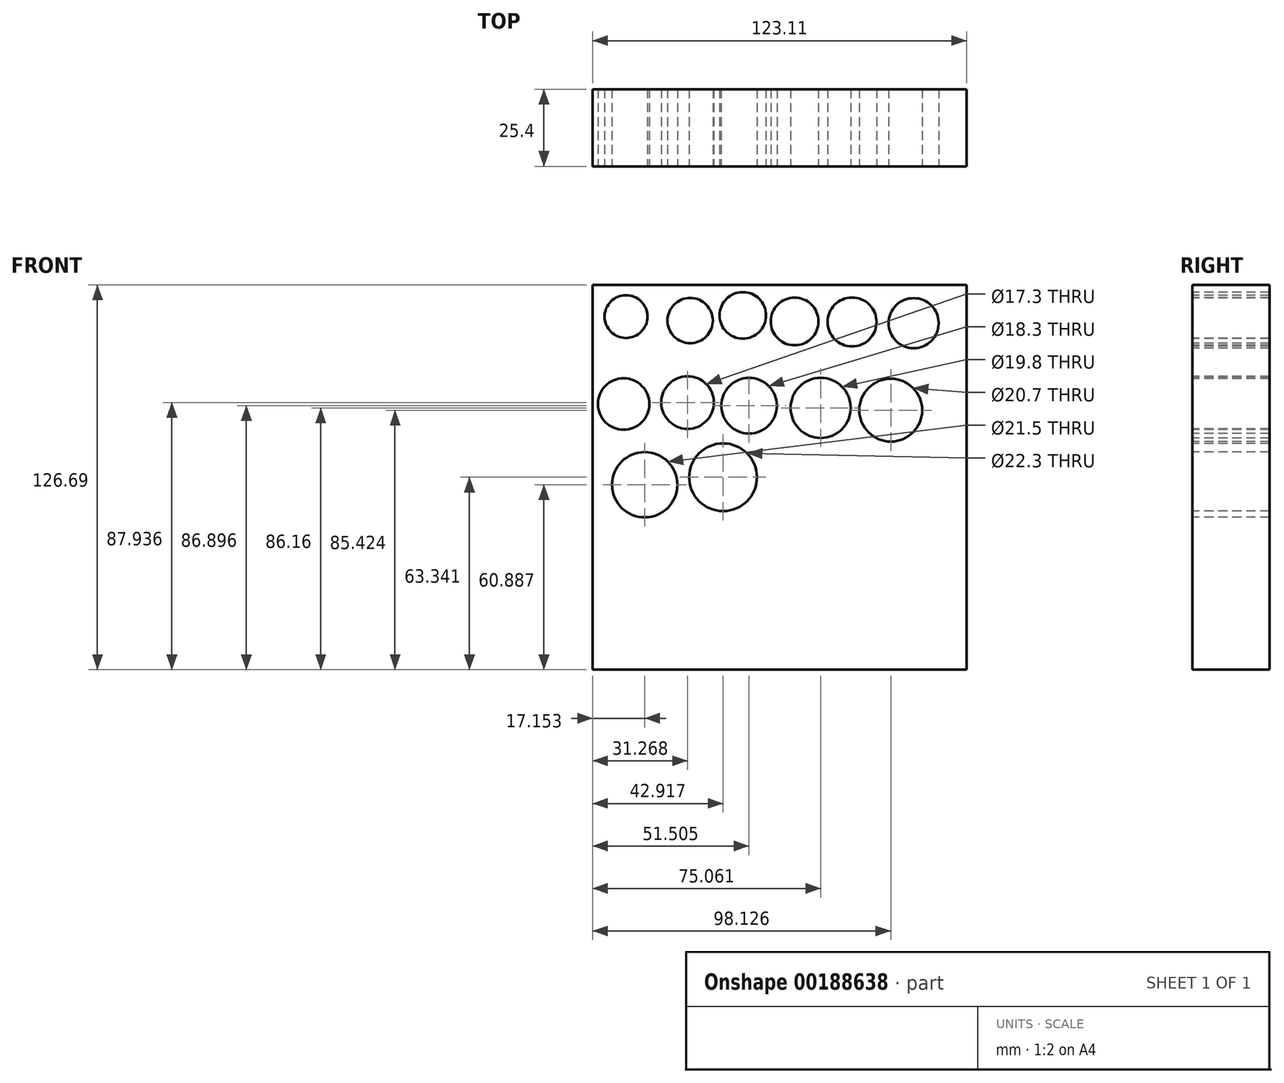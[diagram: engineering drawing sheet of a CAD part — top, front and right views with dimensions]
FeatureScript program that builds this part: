
annotation { "Feature Type Name" : "Feature", "Feature Type Description" : "" }
export const myFeature = defineFeature(function(context is Context, id is Id, definition is map)
    precondition{}
    {
        {
            var Q0;
            Q0=qCreatedBy(makeId("Front.planeOp"),FACE);
            var sketch = newSketch(context, id + "F0", { "sketchPlane" : qUnion([Q0])});
            skLineSegment(sketch, "E0.bottom", {"start": v(-58.66, 60.18) * mm, "end": v(64.45, 60.18) * mm});
            skLineSegment(sketch, "E0.top", {"start": v(-58.66, -66.51) * mm, "end": v(64.45, -66.51) * mm});
            skLineSegment(sketch, "E0.left", {"start": v(-58.66, 60.18) * mm, "end": v(-58.66, -66.51) * mm});
            skLineSegment(sketch, "E0.right", {"start": v(64.45, 60.18) * mm, "end": v(64.45, -66.51) * mm});
            skSolve(sketch);
        }
        {
            var Q0;
            Q0=makeQuery(id+"F0.imprint","IMPRINT",FACE,{"disambiguationData":[TD([[makeQuery(id+"F0.imprint","IMPRINT",EDGE,{"derivedFrom":sQuery(id+"F0.wireOp",EDGE,"E0.bottom")}),-1.0]])]});
            extrude(context, id + "F1", {"entities" : qUnion([Q0]), "depth" : 25.4 * mm});
        }
        {
            var Q0;
            Q0=makeQuery(id+"F1.opExtrude","CAP_FACE",FACE,{"disambiguationData":[OSD([sQuery(id+"F0.wireOp",EDGE,"E0.bottom"),sQuery(id+"F0.wireOp",EDGE,"E0.top"),sQuery(id+"F0.wireOp",EDGE,"E0.left"),sQuery(id+"F0.wireOp",EDGE,"E0.right")])],"isStart":false});
            var sketch = newSketch(context, id + "F2", { "sketchPlane" : qUnion([Q0])});
            skCircle(sketch, "E1", {"center": v(-47.65, 49.71) * mm, "radius": 7.05 * mm});
            skCircle(sketch, "E2", {"center": v(-26.54, 48.4) * mm, "radius": 7.45 * mm});
            skCircle(sketch, "E3", {"center": v(-9.22, 50.1) * mm, "radius": 7.65 * mm});
            skCircle(sketch, "E4", {"center": v(7.81, 48.11) * mm, "radius": 7.85 * mm});
            skCircle(sketch, "E5", {"center": v(26.72, 47.94) * mm, "radius": 8.05 * mm});
            skCircle(sketch, "E6", {"center": v(46.99, 47.55) * mm, "radius": 8.25 * mm});
            skCircle(sketch, "E7", {"center": v(-48.44, 20.94) * mm, "radius": 8.45 * mm});
            skCircle(sketch, "E8", {"center": v(-27.4, 21.43) * mm, "radius": 8.65 * mm});
            skCircle(sketch, "E9", {"center": v(-7.15, 20.39) * mm, "radius": 9.1 * mm});
            skCircle(sketch, "E10", {"center": v(20.57, 18.42) * mm, "radius": 240.03 * mm});
            skCircle(sketch, "E11", {"center": v(16.4, 19.65) * mm, "radius": 9.9 * mm});
            skCircle(sketch, "E12", {"center": v(39.47, 18.91) * mm, "radius": 10.35 * mm});
            skCircle(sketch, "E13", {"center": v(-41.5, -5.62) * mm, "radius": 10.75 * mm});
            skCircle(sketch, "E14", {"center": v(-15.74, -3.17) * mm, "radius": 11.65 * mm});
            skSolve(sketch);
        }
        {
            var Q0;
            Q0=sQuery(id+"F2.wireOp",VERTEX,"E1.center");
            var Q1;
            Q1=makeQuery(id+"F1.opExtrude","SWEPT_BODY",BODY,{"disambiguationData":[OSD([sQuery(id+"F0.wireOp",EDGE,"E0.bottom"),sQuery(id+"F0.wireOp",EDGE,"E0.top"),sQuery(id+"F0.wireOp",EDGE,"E0.left"),sQuery(id+"F0.wireOp",EDGE,"E0.right")])]});
            hole(context, id + "F3", {"style" : HoleStyle.SIMPLE, "endStyle" : HoleEndStyle.THROUGH, "holeDiameter" : 14.1 * mm, "locations" : qUnion([Q0]), "scope" : qUnion([Q1]), "isTappedThrough" : true});
        }
        {
            var Q0;
            Q0=sQuery(id+"F2.wireOp",VERTEX,"E2.center");
            var Q1;
            Q1=makeQuery(id+"F1.opExtrude","SWEPT_BODY",BODY,{"disambiguationData":[OSD([sQuery(id+"F0.wireOp",EDGE,"E0.bottom"),sQuery(id+"F0.wireOp",EDGE,"E0.top"),sQuery(id+"F0.wireOp",EDGE,"E0.left"),sQuery(id+"F0.wireOp",EDGE,"E0.right")])]});
            hole(context, id + "F4", {"style" : HoleStyle.SIMPLE, "endStyle" : HoleEndStyle.THROUGH, "holeDiameter" : 14.9 * mm, "locations" : qUnion([Q0]), "scope" : qUnion([Q1]), "isTappedThrough" : true});
        }
        {
            var Q0;
            Q0=sQuery(id+"F2.wireOp",VERTEX,"E3.center");
            var Q1;
            Q1=makeQuery(id+"F1.opExtrude","SWEPT_BODY",BODY,{"disambiguationData":[OSD([sQuery(id+"F0.wireOp",EDGE,"E0.bottom"),sQuery(id+"F0.wireOp",EDGE,"E0.top"),sQuery(id+"F0.wireOp",EDGE,"E0.left"),sQuery(id+"F0.wireOp",EDGE,"E0.right")])]});
            hole(context, id + "F5", {"style" : HoleStyle.SIMPLE, "endStyle" : HoleEndStyle.THROUGH, "holeDiameter" : 15.3 * mm, "locations" : qUnion([Q0]), "scope" : qUnion([Q1]), "isTappedThrough" : true});
        }
        {
            var Q0;
            Q0=sQuery(id+"F2.wireOp",VERTEX,"E4.center");
            var Q1;
            Q1=makeQuery(id+"F1.opExtrude","SWEPT_BODY",BODY,{"disambiguationData":[OSD([sQuery(id+"F0.wireOp",EDGE,"E0.bottom"),sQuery(id+"F0.wireOp",EDGE,"E0.top"),sQuery(id+"F0.wireOp",EDGE,"E0.left"),sQuery(id+"F0.wireOp",EDGE,"E0.right")])]});
            hole(context, id + "F6", {"style" : HoleStyle.SIMPLE, "endStyle" : HoleEndStyle.THROUGH, "holeDiameter" : 15.7 * mm, "locations" : qUnion([Q0]), "scope" : qUnion([Q1]), "isTappedThrough" : true});
        }
        {
            var Q0;
            Q0=sQuery(id+"F2.wireOp",VERTEX,"E5.center");
            var Q1;
            Q1=makeQuery(id+"F1.opExtrude","SWEPT_BODY",BODY,{"disambiguationData":[OSD([sQuery(id+"F0.wireOp",EDGE,"E0.bottom"),sQuery(id+"F0.wireOp",EDGE,"E0.top"),sQuery(id+"F0.wireOp",EDGE,"E0.left"),sQuery(id+"F0.wireOp",EDGE,"E0.right")])]});
            hole(context, id + "F7", {"style" : HoleStyle.SIMPLE, "endStyle" : HoleEndStyle.THROUGH, "holeDiameter" : 16.1 * mm, "locations" : qUnion([Q0]), "scope" : qUnion([Q1]), "isTappedThrough" : true});
        }
        {
            var Q0;
            Q0=sQuery(id+"F2.wireOp",VERTEX,"E6.center");
            var Q1;
            Q1=makeQuery(id+"F1.opExtrude","SWEPT_BODY",BODY,{"disambiguationData":[OSD([sQuery(id+"F0.wireOp",EDGE,"E0.bottom"),sQuery(id+"F0.wireOp",EDGE,"E0.top"),sQuery(id+"F0.wireOp",EDGE,"E0.left"),sQuery(id+"F0.wireOp",EDGE,"E0.right")])]});
            hole(context, id + "F8", {"style" : HoleStyle.SIMPLE, "endStyle" : HoleEndStyle.THROUGH, "holeDiameter" : 16.5 * mm, "locations" : qUnion([Q0]), "scope" : qUnion([Q1]), "isTappedThrough" : true});
        }
        {
            var Q0;
            Q0=sQuery(id+"F2.wireOp",VERTEX,"E7.center");
            var Q1;
            Q1=makeQuery(id+"F1.opExtrude","SWEPT_BODY",BODY,{"disambiguationData":[OSD([sQuery(id+"F0.wireOp",EDGE,"E0.bottom"),sQuery(id+"F0.wireOp",EDGE,"E0.top"),sQuery(id+"F0.wireOp",EDGE,"E0.left"),sQuery(id+"F0.wireOp",EDGE,"E0.right")])]});
            hole(context, id + "F9", {"style" : HoleStyle.SIMPLE, "endStyle" : HoleEndStyle.THROUGH, "holeDiameter" : 16.9 * mm, "locations" : qUnion([Q0]), "scope" : qUnion([Q1]), "isTappedThrough" : true});
        }
        {
            var Q0;
            Q0=sQuery(id+"F2.wireOp",VERTEX,"E8.center");
            var Q1;
            Q1=makeQuery(id+"F1.opExtrude","SWEPT_BODY",BODY,{"disambiguationData":[OSD([sQuery(id+"F0.wireOp",EDGE,"E0.bottom"),sQuery(id+"F0.wireOp",EDGE,"E0.top"),sQuery(id+"F0.wireOp",EDGE,"E0.left"),sQuery(id+"F0.wireOp",EDGE,"E0.right")])]});
            hole(context, id + "F10", {"style" : HoleStyle.SIMPLE, "endStyle" : HoleEndStyle.THROUGH, "holeDiameter" : 17.3 * mm, "locations" : qUnion([Q0]), "scope" : qUnion([Q1]), "isTappedThrough" : true});
        }
        {
            var Q0;
            Q0=sQuery(id+"F2.wireOp",VERTEX,"E9.center");
            var Q1;
            Q1=makeQuery(id+"F1.opExtrude","SWEPT_BODY",BODY,{"disambiguationData":[OSD([sQuery(id+"F0.wireOp",EDGE,"E0.bottom"),sQuery(id+"F0.wireOp",EDGE,"E0.top"),sQuery(id+"F0.wireOp",EDGE,"E0.left"),sQuery(id+"F0.wireOp",EDGE,"E0.right")])]});
            hole(context, id + "F11", {"style" : HoleStyle.SIMPLE, "endStyle" : HoleEndStyle.THROUGH, "holeDiameter" : 18.3 * mm, "locations" : qUnion([Q0]), "scope" : qUnion([Q1]), "isTappedThrough" : true});
        }
        {
            var Q0;
            Q0=sQuery(id+"F2.wireOp",VERTEX,"E11.center");
            var Q1;
            Q1=makeQuery(id+"F1.opExtrude","SWEPT_BODY",BODY,{"disambiguationData":[OSD([sQuery(id+"F0.wireOp",EDGE,"E0.bottom"),sQuery(id+"F0.wireOp",EDGE,"E0.top"),sQuery(id+"F0.wireOp",EDGE,"E0.left"),sQuery(id+"F0.wireOp",EDGE,"E0.right")])]});
            hole(context, id + "F12", {"style" : HoleStyle.SIMPLE, "endStyle" : HoleEndStyle.THROUGH, "holeDiameter" : 19.8 * mm, "locations" : qUnion([Q0]), "scope" : qUnion([Q1]), "isTappedThrough" : true});
        }
        {
            var Q0;
            Q0=sQuery(id+"F2.wireOp",VERTEX,"E12.center");
            var Q1;
            Q1=makeQuery(id+"F1.opExtrude","SWEPT_BODY",BODY,{"disambiguationData":[OSD([sQuery(id+"F0.wireOp",EDGE,"E0.bottom"),sQuery(id+"F0.wireOp",EDGE,"E0.top"),sQuery(id+"F0.wireOp",EDGE,"E0.left"),sQuery(id+"F0.wireOp",EDGE,"E0.right")])]});
            hole(context, id + "F13", {"style" : HoleStyle.SIMPLE, "endStyle" : HoleEndStyle.THROUGH, "holeDiameter" : 20.7 * mm, "locations" : qUnion([Q0]), "scope" : qUnion([Q1]), "isTappedThrough" : true});
        }
        {
            var Q0;
            Q0=sQuery(id+"F2.wireOp",VERTEX,"E13.center");
            var Q1;
            Q1=makeQuery(id+"F1.opExtrude","SWEPT_BODY",BODY,{"disambiguationData":[OSD([sQuery(id+"F0.wireOp",EDGE,"E0.bottom"),sQuery(id+"F0.wireOp",EDGE,"E0.top"),sQuery(id+"F0.wireOp",EDGE,"E0.left"),sQuery(id+"F0.wireOp",EDGE,"E0.right")])]});
            hole(context, id + "F14", {"style" : HoleStyle.SIMPLE, "endStyle" : HoleEndStyle.THROUGH, "holeDiameter" : 21.5 * mm, "locations" : qUnion([Q0]), "scope" : qUnion([Q1]), "isTappedThrough" : true});
        }
        {
            var Q0;
            Q0=sQuery(id+"F2.wireOp",VERTEX,"E14.center");
            var Q1;
            Q1=makeQuery(id+"F1.opExtrude","SWEPT_BODY",BODY,{"disambiguationData":[OSD([sQuery(id+"F0.wireOp",EDGE,"E0.bottom"),sQuery(id+"F0.wireOp",EDGE,"E0.top"),sQuery(id+"F0.wireOp",EDGE,"E0.left"),sQuery(id+"F0.wireOp",EDGE,"E0.right")])]});
            hole(context, id + "F15", {"style" : HoleStyle.SIMPLE, "endStyle" : HoleEndStyle.THROUGH, "holeDiameter" : 22.3 * mm, "locations" : qUnion([Q0]), "scope" : qUnion([Q1]), "isTappedThrough" : true});
        }
    });
